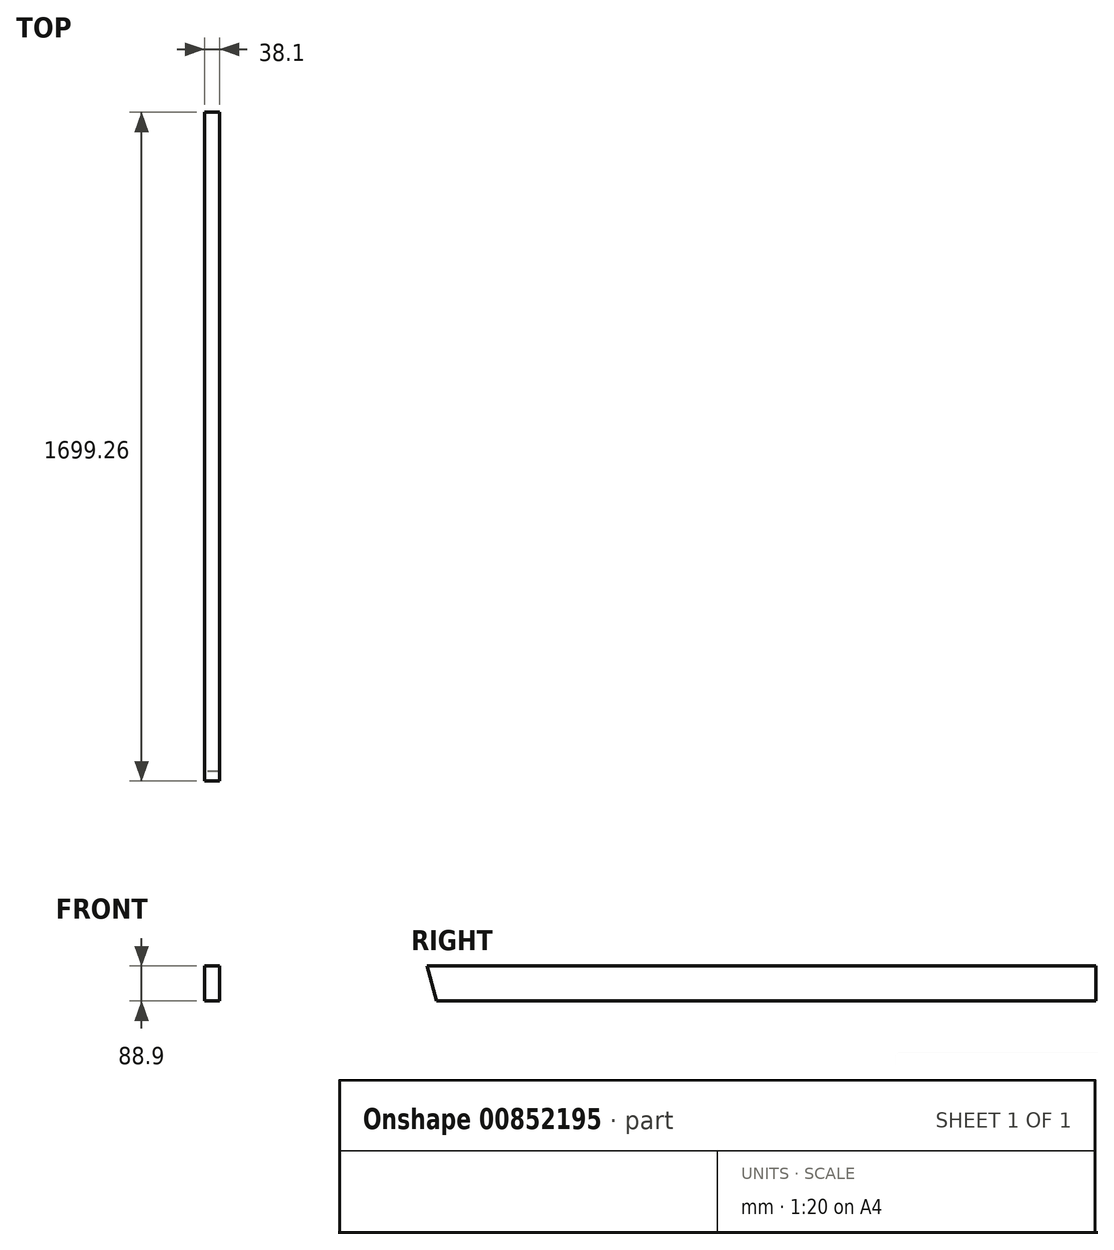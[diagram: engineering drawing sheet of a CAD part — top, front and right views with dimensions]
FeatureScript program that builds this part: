
annotation { "Feature Type Name" : "Feature", "Feature Type Description" : "" }
export const myFeature = defineFeature(function(context is Context, id is Id, definition is map)
    precondition{}
    {
        {
            var Q0;
            Q0=qCreatedBy(makeId("Front.planeOp"),FACE);
            var sketch = newSketch(context, id + "F0", { "sketchPlane" : qUnion([Q0])});
            skLineSegment(sketch, "E0.bottom", {"start": v(19.05, -44.45) * mm, "end": v(-19.05, -44.45) * mm});
            skLineSegment(sketch, "E0.top", {"start": v(19.05, 44.45) * mm, "end": v(-19.05, 44.45) * mm});
            skLineSegment(sketch, "E0.left", {"start": v(19.05, -44.45) * mm, "end": v(19.05, 44.45) * mm});
            skLineSegment(sketch, "E0.right", {"start": v(-19.05, -44.45) * mm, "end": v(-19.05, 44.45) * mm});
            skPoint(sketch, "E0.middle", {"position": v(0, 0) * mm});
            skSolve(sketch);
        }
        {
            var Q0;
            Q0=makeQuery(id+"F0.imprint","IMPRINT",FACE,{"disambiguationData":[TD([[makeQuery(id+"F0.imprint","IMPRINT",EDGE,{"derivedFrom":sQuery(id+"F0.wireOp",EDGE,"E0.bottom")}),-1.0]])]});
            extrude(context, id + "F1", {"entities" : qUnion([Q0]), "depth" : 1699.26 * mm, "offsetDistance" : 25.4 * mm});
        }
        {
            var Q0;
            Q0=qCreatedBy(makeId("Right.planeOp"),FACE);
            var sketch = newSketch(context, id + "F2", { "sketchPlane" : qUnion([Q0])});
            skLineSegment(sketch, "E1", {"start": v(-1699.26, 44.45) * mm, "end": v(-1699.26, -44.45) * mm});
            skLineSegment(sketch, "E2", {"start": v(-1699.26, -44.45) * mm, "end": v(-1675.38, -44.45) * mm});
            skLineSegment(sketch, "E3", {"start": v(-1675.38, -44.45) * mm, "end": v(-1699.26, 44.45) * mm});
            skSolve(sketch);
        }
        {
            var Q0;
            Q0=qSketchRegion(id+"F2",true);
            extrude(context, id + "F3", {"entities" : qUnion([Q0]), "operationType" : NewBodyOperationType.REMOVE, "endBound" : BoundingType.SYMMETRIC, "depth" : 50.8 * mm, "offsetDistance" : 25.4 * mm});
        }
    });
